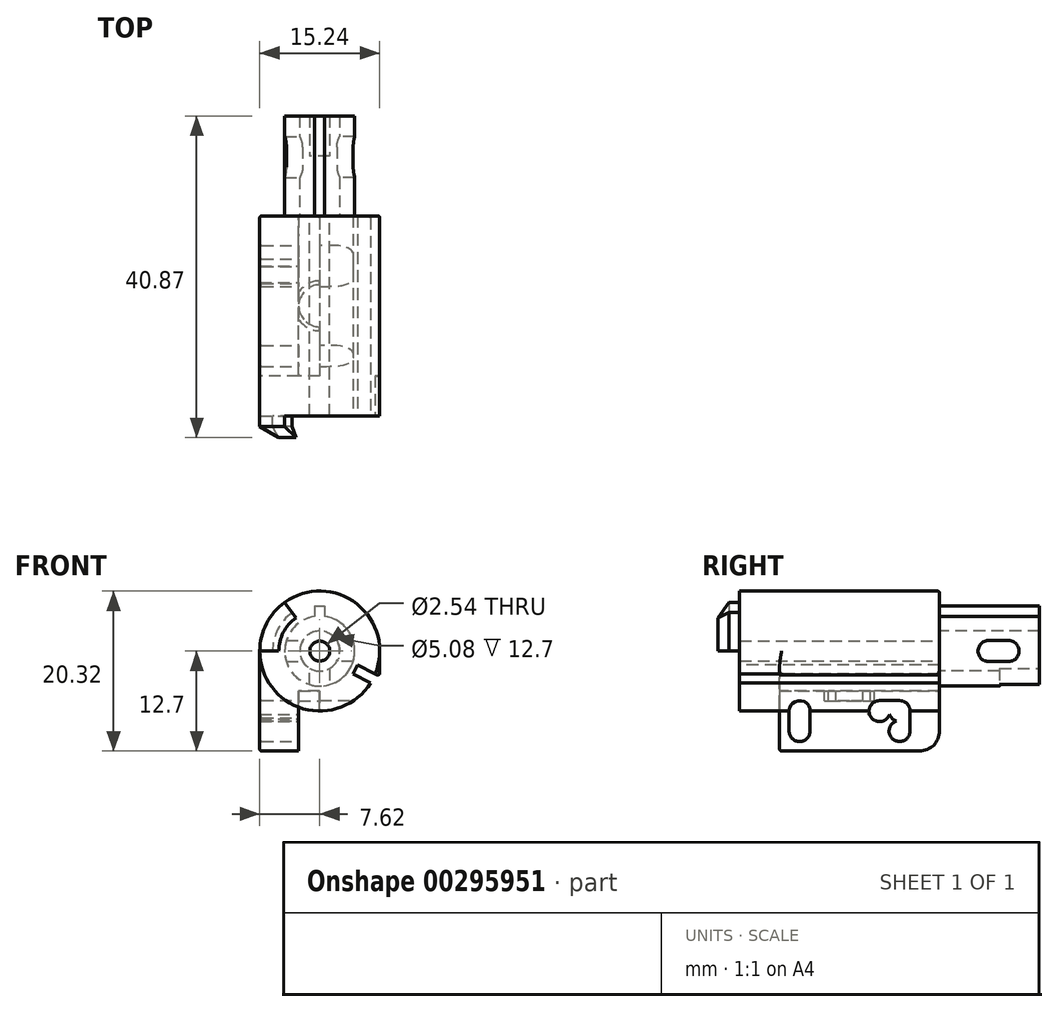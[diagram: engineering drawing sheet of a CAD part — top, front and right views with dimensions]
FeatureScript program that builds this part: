
annotation { "Feature Type Name" : "Feature", "Feature Type Description" : "" }
export const myFeature = defineFeature(function(context is Context, id is Id, definition is map)
    precondition{}
    {
        {
            var Q0;
            Q0=qCreatedBy(makeId("Front.planeOp"),FACE);
            var sketch = newSketch(context, id + "F0", { "sketchPlane" : qUnion([Q0])});
            skPoint(sketch, "E0.middle", {"position": v(0, 0) * mm});
            skLineSegment(sketch, "E1.bottom", {"start": v(7.62, 37.7) * mm, "end": v(-7.62, 37.7) * mm});
            skLineSegment(sketch, "E1.top", {"start": v(7.62, -37.7) * mm, "end": v(-7.62, -37.7) * mm});
            skLineSegment(sketch, "E1.left", {"start": v(7.62, 37.7) * mm, "end": v(7.62, -37.7) * mm});
            skLineSegment(sketch, "E1.right", {"start": v(-7.62, 37.7) * mm, "end": v(-7.62, -37.7) * mm});
            skCircle(sketch, "E2", {"center": v(0, 0) * mm, "radius": 7.62 * mm});
            skCircle(sketch, "E3", {"center": v(0, 0) * mm, "radius": 1.27 * mm});
            skSolve(sketch);
        }
        {
            var Q0;
            Q0=makeQuery(id+"F0.imprint","IMPRINT",FACE,{"disambiguationData":[TD([[makeQuery(id+"F0.imprint","IMPRINT",EDGE,{"derivedFrom":sQuery(id+"F0.wireOp",EDGE,"E3")}),-1.0]])]});
            extrude(context, id + "F1", {"entities" : qUnion([Q0]), "depth" : 12.7 * mm});
        }
        {
            var Q0;
            Q0=makeQuery(id+"F1.opExtrude","CAP_FACE",FACE,{"disambiguationData":[OSD([sQuery(id+"F0.wireOp",EDGE,"E2"),sQuery(id+"F0.wireOp",EDGE,"E3")])],"isStart":false});
            var sketch = newSketch(context, id + "F2", { "sketchPlane" : qUnion([Q0])});
            skArc(sketch, "E4", {"start": v(-7.62, 0) * mm, "mid": v(-6.78, 3.48) * mm, "end": v(-4.44, 6.2) * mm});
            skArc(sketch, "E5.0", {"start": v(-6, 0) * mm, "mid": v(-5.34, 2.74) * mm, "end": v(-3.5, 4.88) * mm});
            skLineSegment(sketch, "E6", {"start": v(-4.44, 6.2) * mm, "end": v(-3.5, 4.88) * mm});
            skLineSegment(sketch, "E7", {"start": v(-7.62, 0) * mm, "end": v(-6, 0) * mm});
            skSolve(sketch);
        }
        {
            var Q0;
            Q0=qSketchRegion(id+"F2",true);
            extrude(context, id + "F3", {"entities" : qUnion([Q0]), "operationType" : NewBodyOperationType.ADD, "depth" : 1.37 * mm});
        }
        {
            var Q0;
            Q0=makeQuery(id+"F3.opExtrude","CAP_FACE",FACE,{"disambiguationData":[OSD([sQuery(id+"F2.wireOp",EDGE,"E4"),sQuery(id+"F2.wireOp",EDGE,"E5.0"),sQuery(id+"F2.wireOp",EDGE,"E6"),sQuery(id+"F2.wireOp",EDGE,"E7")])],"isStart":false});
            cPlane(context, id + "F4", {"entities" : qUnion([Q0]), "cplaneType" : CPlaneType.OFFSET, "offset" : 1.4 * mm, "width" : 152.4 * mm, "height" : 152.4 * mm});
        }
        {
            var Q0;
            Q0=qCreatedBy(id+"F4.planeOp",FACE);
            var sketch = newSketch(context, id + "F5", { "sketchPlane" : qUnion([Q0])});
            skArc(sketch, "E8.0", {"start": v(-3.04, 4.23) * mm, "mid": v(-4.63, 2.38) * mm, "end": v(-5.2, 0) * mm});
            skSolve(sketch);
        }
        {
            var Q0;
            Q0=makeQuery(id+"F3.opExtrude","CAP_VERTEX",VERTEX,{"disambiguationData":[OSD([sQuery(id+"F0.wireOp",EDGE,"E2"),sQuery(id+"F2.wireOp",EDGE,"E4"),sQuery(id+"F2.wireOp",EDGE,"E7")])],"isStart":false});
            var Q1;
            Q1=makeQuery(id+"F3.opExtrude","CAP_VERTEX",VERTEX,{"disambiguationData":[OSD([sQuery(id+"F2.wireOp",EDGE,"E5.0"),sQuery(id+"F2.wireOp",EDGE,"E7")])],"isStart":false});
            var Q2;
            Q2=sQuery(id+"F5.wireOp",VERTEX,"E8.0.end");
            cPlane(context, id + "F6", {"entities" : qUnion([Q0, Q1, Q2]), "cplaneType" : CPlaneType.THREE_POINT, "offset" : 25.4 * mm, "width" : 152.4 * mm, "height" : 152.4 * mm});
        }
        {
            var Q0;
            Q0=qCreatedBy(id+"F6.planeOp",FACE);
            var sketch = newSketch(context, id + "F7", { "sketchPlane" : qUnion([Q0])});
            skPoint(sketch, "E9.0", {"position": v(-7.62, -14.07) * mm});
            skPoint(sketch, "E10.0", {"position": v(-6, -14.07) * mm});
            skPoint(sketch, "E11.0", {"position": v(-5.2, -15.47) * mm});
            skLineSegment(sketch, "E12", {"start": v(-7.62, -14.07) * mm, "end": v(-5.2, -15.47) * mm});
            skLineSegment(sketch, "E13", {"start": v(-5.2, -15.47) * mm, "end": v(-6, -14.07) * mm});
            skLineSegment(sketch, "E14", {"start": v(-6, -14.07) * mm, "end": v(-7.62, -14.07) * mm});
            skSolve(sketch);
        }
        {
            var Q0;
            Q0=makeQuery(id+"F3.opExtrude","CAP_VERTEX",VERTEX,{"disambiguationData":[OSD([sQuery(id+"F0.wireOp",EDGE,"E2"),sQuery(id+"F2.wireOp",EDGE,"E4"),sQuery(id+"F2.wireOp",EDGE,"E6")])],"isStart":false});
            var Q1;
            Q1=makeQuery(id+"F3.opExtrude","CAP_VERTEX",VERTEX,{"disambiguationData":[OSD([sQuery(id+"F2.wireOp",EDGE,"E5.0"),sQuery(id+"F2.wireOp",EDGE,"E6")])],"isStart":false});
            var Q2;
            Q2=sQuery(id+"F5.wireOp",VERTEX,"E8.0.start");
            cPlane(context, id + "F8", {"entities" : qUnion([Q0, Q1, Q2]), "cplaneType" : CPlaneType.THREE_POINT, "offset" : 25.4 * mm, "width" : 152.4 * mm, "height" : 152.4 * mm});
        }
        {
            var Q0;
            Q0=qCreatedBy(id+"F8.planeOp",FACE);
            var sketch = newSketch(context, id + "F9", { "sketchPlane" : qUnion([Q0])});
            skPoint(sketch, "E15.0", {"position": v(-14.07, 7.62) * mm});
            skPoint(sketch, "E16.0", {"position": v(-14.07, 6) * mm});
            skPoint(sketch, "E17.0", {"position": v(-15.47, 5.2) * mm});
            skLineSegment(sketch, "E18", {"start": v(-14.07, 7.62) * mm, "end": v(-14.07, 6) * mm});
            skLineSegment(sketch, "E19", {"start": v(-14.07, 6) * mm, "end": v(-15.47, 5.2) * mm});
            skLineSegment(sketch, "E20", {"start": v(-15.47, 5.2) * mm, "end": v(-14.07, 7.62) * mm});
            skSolve(sketch);
        }
        {
            var Q0;
            Q0=makeQuery(id+"F7.imprint","IMPRINT",FACE,{"disambiguationData":[TD([[makeQuery(id+"F7.imprint","IMPRINT",EDGE,{"derivedFrom":sQuery(id+"F7.wireOp",EDGE,"E12")}),1.0]])]});
            var Q1;
            Q1=makeQuery(id+"F9.imprint","IMPRINT",FACE,{"disambiguationData":[TD([[makeQuery(id+"F9.imprint","IMPRINT",EDGE,{"derivedFrom":sQuery(id+"F9.wireOp",EDGE,"E18")}),-1.0]])]});
            var Q2;
            Q2=makeQuery(id+"F7.imprint","IMPRINT",FACE,{"disambiguationData":[TD([[makeQuery(id+"F7.imprint","IMPRINT",EDGE,{"derivedFrom":sQuery(id+"F7.wireOp",EDGE,"E12")}),1.0]])]});
            var Q3;
            Q3=makeQuery(id+"F9.imprint","IMPRINT",FACE,{"disambiguationData":[TD([[makeQuery(id+"F9.imprint","IMPRINT",EDGE,{"derivedFrom":sQuery(id+"F9.wireOp",EDGE,"E18")}),-1.0]])]});
            var Q4;
            Q4=makeQuery(id+"F3.opExtrude","CAP_EDGE",EDGE,{"disambiguationData":[OSD([sQuery(id+"F2.wireOp",EDGE,"E4")])],"isStart":false});
            var Q5;
            Q5=makeQuery(id+"F3.opExtrude","CAP_EDGE",EDGE,{"disambiguationData":[OSD([sQuery(id+"F2.wireOp",EDGE,"E5.0")])],"isStart":false});
            var Q6;
            Q6=sQuery(id+"F5.wireOp",EDGE,"E8.0");
            loft(context, id + "F10", {"addGuides" : true, "sheetProfilesArray" : [{ "sheetProfileEntities" : qUnion([Q0]) }, { "sheetProfileEntities" : qUnion([Q1]) }], "wireProfilesArray" : [{ "wireProfileEntities" : qUnion([Q2]) }, { "wireProfileEntities" : qUnion([Q3]) }], "guidesArray" : [{ "guideEntities" : qUnion([Q4]), "guideDerivativeType" : LoftGuideDerivativeType.DEFAULT, "guideDerivativeMagnitude" : 1 }, { "guideEntities" : qUnion([Q5]), "guideDerivativeType" : LoftGuideDerivativeType.DEFAULT, "guideDerivativeMagnitude" : 1 }, { "guideEntities" : qUnion([Q6]), "guideDerivativeType" : LoftGuideDerivativeType.DEFAULT, "guideDerivativeMagnitude" : 1 }]});
        }
        {
            var Q0;
            Q0=makeQuery(id+"F1.opExtrude","CAP_FACE",FACE,{"disambiguationData":[OSD([sQuery(id+"F0.wireOp",EDGE,"E2"),sQuery(id+"F0.wireOp",EDGE,"E3")])],"isStart":true});
            var sketch = newSketch(context, id + "F11", { "sketchPlane" : qUnion([Q0])});
            skArc(sketch, "E21.0", {"start": v(-4.16, -6.39) * mm, "mid": v(-6.39, 4.16) * mm, "end": v(4.16, 6.39) * mm});
            skCircle(sketch, "E22", {"center": v(0, 0) * mm, "radius": 7.62 * mm});
            skSolve(sketch);
        }
        {
            var Q0;
            Q0=makeQuery(id+"F11.imprint","IMPRINT",FACE,{"disambiguationData":[TD([[makeQuery(id+"F11.imprint","IMPRINT",EDGE,{"derivedFrom":sQuery(id+"F11.wireOp",EDGE,"E22")}),1.0]])]});
            var Q1;
            Q1=makeQuery(id+"F11.imprint","IMPRINT",FACE,{"disambiguationData":[TD([[makeQuery(id+"F11.imprint","IMPRINT",EDGE,{"derivedFrom":makeQuery(id+"F1.opExtrude","CAP_EDGE",EDGE,{"disambiguationData":[OSD([sQuery(id+"F0.wireOp",EDGE,"E2")])],"isStart":true})}),-1.0]])]});
            var Q2;
            Q2=makeQuery(id+"F11.imprint","IMPRINT",FACE,{"disambiguationData":[TD([[makeQuery(id+"F11.imprint","IMPRINT",EDGE,{"derivedFrom":sQuery(id+"F11.wireOp",EDGE,"E22")}),-1.0]])]});
            extrude(context, id + "F12", {"entities" : qUnion([Q0, Q1, Q2]), "depth" : 12.7 * mm});
        }
        {
            var Q0;
            Q0=makeQuery(id+"FqKjOTA0KTiobea_0.opExtrude","SWEPT_BODY",BODY,{"disambiguationData":[OSD([sQuery(id+"F0.wireOp",EDGE,"uHF2WHmJ-zJ7i-FEed-3bSX-mTsy0IzEVw90"),sQuery(id+"F0.wireOp",EDGE,"k3DuiY5w-GI1o-rOdS-LLCr-VDr8IVeulzbr"),sQuery(id+"F0.wireOp",EDGE,"E1.left"),sQuery(id+"F0.wireOp",EDGE,"E1.right")])]});
            var Q1;
            Q1=makeQuery(id+"F1.opExtrude","SWEPT_BODY",BODY,{"disambiguationData":[OSD([sQuery(id+"F0.wireOp",EDGE,"E2"),sQuery(id+"F0.wireOp",EDGE,"E3")])]});
            var Q2;
            Q2=makeQuery(id+"F10.opLoft","SWEPT_BODY",BODY,{"disambiguationData":[OSD([sQuery(id+"F2.wireOp",EDGE,"E4"),sQuery(id+"F2.wireOp",EDGE,"E5.0"),sQuery(id+"F5.wireOp",EDGE,"E8.0"),makeQuery(id+"F7.imprint","IMPRINT",FACE,{"disambiguationData":[TD([[makeQuery(id+"F7.imprint","IMPRINT",EDGE,{"derivedFrom":sQuery(id+"F7.wireOp",EDGE,"E12")}),1.0]])]}),makeQuery(id+"F9.imprint","IMPRINT",FACE,{"disambiguationData":[TD([[makeQuery(id+"F9.imprint","IMPRINT",EDGE,{"derivedFrom":sQuery(id+"F9.wireOp",EDGE,"E18")}),-1.0]])]})])]});
            var Q3;
            Q3=makeQuery(id+"F12.opExtrude","SWEPT_BODY",BODY,{"disambiguationData":[OSD([sQuery(id+"F0.wireOp",EDGE,"E3"),sQuery(id+"F11.wireOp",EDGE,"E22")])]});
            booleanBodies(context, id + "F13", {"operationType" : BooleanOperationType.UNION, "tools" : qUnion([Q0, Q1, Q2, Q3])});
        }
        {
            var Q0;
            Q0=makeQuery(id+"F12.opExtrude","CAP_FACE",FACE,{"disambiguationData":[OSD([sQuery(id+"F0.wireOp",EDGE,"E3"),sQuery(id+"F11.wireOp",EDGE,"E22")])],"isStart":false});
            var sketch = newSketch(context, id + "F14", { "sketchPlane" : qUnion([Q0])});
            skCircle(sketch, "E23", {"center": v(0, 0) * mm, "radius": 7.62 * mm});
            skSolve(sketch);
        }
        {
            var Q0;
            Q0=makeQuery(id+"F14.imprint","IMPRINT",FACE,{"disambiguationData":[TD([[makeQuery(id+"F14.imprint","IMPRINT",EDGE,{"derivedFrom":sQuery(id+"F14.wireOp",EDGE,"E23")}),-1.0]])]});
            var sketch = newSketch(context, id + "F15", { "sketchPlane" : qUnion([Q0])});
            skCircle(sketch, "E24", {"center": v(0, 0) * mm, "radius": 4.45 * mm});
            skCircle(sketch, "E25", {"center": v(0, 0) * mm, "radius": 2.54 * mm});
            skSolve(sketch);
        }
        {
            var Q0;
            Q0=makeQuery(id+"F15.imprint","IMPRINT",FACE,{"disambiguationData":[TD([[makeQuery(id+"F15.imprint","IMPRINT",EDGE,{"derivedFrom":sQuery(id+"F15.wireOp",EDGE,"E24")}),1.0]])]});
            var Q1;
            Q1=qSketchRegion(id+"F17",true);
            extrude(context, id + "F16", {"entities" : qUnion([Q0, Q1]), "operationType" : NewBodyOperationType.ADD, "depth" : 12.7 * mm});
        }
        {
            var Q0;
            Q0=qCreatedBy(makeId("Right.planeOp"),FACE);
            var sketch = newSketch(context, id + "F17", { "sketchPlane" : qUnion([Q0])});
            skArc(sketch, "E26", {"start": v(18.92, 1.33) * mm, "mid": v(17.59, 0) * mm, "end": v(18.92, -1.33) * mm});
            skArc(sketch, "E27", {"start": v(21.46, -1.33) * mm, "mid": v(22.8, 0) * mm, "end": v(21.46, 1.33) * mm});
            skLineSegment(sketch, "E28", {"start": v(21.46, 0) * mm, "end": v(21.46, 1.33) * mm});
            skLineSegment(sketch, "E29", {"start": v(21.46, 1.33) * mm, "end": v(18.92, 1.33) * mm});
            skLineSegment(sketch, "E30", {"start": v(18.92, 1.33) * mm, "end": v(18.92, 0) * mm});
            skLineSegment(sketch, "E31", {"start": v(21.46, 0) * mm, "end": v(21.46, -1.33) * mm});
            skLineSegment(sketch, "E32", {"start": v(21.46, -1.33) * mm, "end": v(18.92, -1.33) * mm});
            skLineSegment(sketch, "E33", {"start": v(18.92, -1.33) * mm, "end": v(18.92, 0) * mm});
            skSolve(sketch);
        }
        {
            var Q0;
            Q0 = qSketchRegion(id + "F17", true);
            extrude(context, id + "F18", {"entities" : qUnion([Q0]), "operationType" : NewBodyOperationType.REMOVE, "oppositeDirection" : true, "depth" : 25.4 * mm});
        }
        {
            var Q0;
            Q0 = qSketchRegion(id + "F17", true);
            var Q1;
            {var subQ0=sQuery(id+"F17.wireOp",EDGE,"E27");var subQ1=sQuery(id+"F17.wireOp",EDGE,"E26");var subQ2=makeQuery(id+"F17.imprint","INTERSECT",VERTEX,{"disambiguationData":[OD(0.0)],"derivedFrom":[subQ1,subQ0]});Q1=makeQuery(id+"F17.imprint","IMPRINT",FACE,{"disambiguationData":[TD([[makeQuery(id+"F17.imprint","IMPRINT",EDGE,{"disambiguationData":[TD([[subQ2,1.0]])],"derivedFrom":subQ1}),1.0]])]});}
            extrude(context, id + "F19", {"entities" : qUnion([Q0, Q1]), "operationType" : NewBodyOperationType.REMOVE, "depth" : 25.4 * mm});
        }
        {
            var Q0;
            Q0=makeQuery(id+"F16.opExtrude","CAP_FACE",FACE,{"disambiguationData":[OSD([sQuery(id+"F15.wireOp",EDGE,"E24"),sQuery(id+"F15.wireOp",EDGE,"E25")])],"isStart":false});
            var sketch = newSketch(context, id + "F20", { "sketchPlane" : qUnion([Q0])});
            skLineSegment(sketch, "E34", {"start": v(0, -2.54) * mm, "end": v(0, -4.45) * mm});
            skLineSegment(sketch, "E35", {"start": v(0, -4.45) * mm, "end": v(-1.27, -4.45) * mm});
            skLineSegment(sketch, "E36", {"start": v(-1.27, -4.45) * mm, "end": v(1.27, -4.45) * mm});
            skLineSegment(sketch, "E37", {"start": v(1.27, -4.45) * mm, "end": v(1.27, -2.2) * mm});
            skLineSegment(sketch, "E38", {"start": v(1.27, -2.2) * mm, "end": v(-1.27, -2.2) * mm});
            skLineSegment(sketch, "E39", {"start": v(-1.27, -2.2) * mm, "end": v(-1.27, -4.45) * mm});
            skSolve(sketch);
        }
        {
            var Q0;
            {var subQ0=sQuery(id+"F20.wireOp",EDGE,"E36");var subQ3=sQuery(id+"F20.wireOp",EDGE,"E39");var subQ4=makeQuery(id+"F20.imprint","INTERSECT",VERTEX,{"derivedFrom":[subQ0,subQ3]});Q0=makeQuery(id+"F20.imprint","IMPRINT",FACE,{"disambiguationData":[TD([[makeQuery(id+"F20.imprint","IMPRINT",EDGE,{"disambiguationData":[TD([[subQ4,1.0]])],"derivedFrom":subQ3}),1.0]])]});}
            var Q1;
            {var subQ0=sQuery(id+"F20.wireOp",EDGE,"E36");var subQ3=sQuery(id+"F20.wireOp",EDGE,"E37");var subQ4=makeQuery(id+"F20.imprint","INTERSECT",VERTEX,{"derivedFrom":[subQ0,subQ3]});Q1=makeQuery(id+"F20.imprint","IMPRINT",FACE,{"disambiguationData":[TD([[makeQuery(id+"F20.imprint","IMPRINT",EDGE,{"disambiguationData":[TD([[subQ4,-1.0]])],"derivedFrom":subQ3}),1.0]])]});}
            var Q2;
            {var subQ0=sQuery(id+"F20.wireOp",EDGE,"E38");Q2=makeQuery(id+"F20.imprint","IMPRINT",FACE,{"disambiguationData":[TD([[makeQuery(id+"F20.imprint","IMPRINT",EDGE,{"derivedFrom":subQ0}),1.0]])]});}
            var Q3;
            {var subQ0=sQuery(id+"F20.wireOp",EDGE,"E34");Q3=makeQuery(id+"F20.imprint","IMPRINT",FACE,{"disambiguationData":[TD([[makeQuery(id+"F20.imprint","IMPRINT",EDGE,{"derivedFrom":subQ0}),1.0]])]});}
            var Q4;
            {var subQ0=sQuery(id+"F20.wireOp",EDGE,"E34");Q4=makeQuery(id+"F20.imprint","IMPRINT",FACE,{"disambiguationData":[TD([[makeQuery(id+"F20.imprint","IMPRINT",EDGE,{"derivedFrom":subQ0}),-1.0]])]});}
            extrude(context, id + "F21", {"entities" : qUnion([Q0, Q1, Q2, Q3, Q4]), "operationType" : NewBodyOperationType.REMOVE, "oppositeDirection" : true, "depth" : 5.08 * mm});
        }
        {
            var Q0;
            Q0=makeQuery(id+"F16.opExtrude","CAP_FACE",FACE,{"disambiguationData":[OSD([sQuery(id+"F15.wireOp",EDGE,"E24"),sQuery(id+"F15.wireOp",EDGE,"E25")])],"isStart":false});
            var sketch = newSketch(context, id + "F22", { "sketchPlane" : qUnion([Q0])});
            skLineSegment(sketch, "E40", {"start": v(0, 4.45) * mm, "end": v(0, 5.72) * mm});
            skPoint(sketch, "E40.endSnap0", {"position": v(0, 4.45) * mm});
            skLineSegment(sketch, "E41", {"start": v(0, 5.72) * mm, "end": v(0.64, 5.72) * mm});
            skLineSegment(sketch, "E42", {"start": v(0.64, 5.72) * mm, "end": v(-0.64, 5.72) * mm});
            skLineSegment(sketch, "E43", {"start": v(-0.64, 5.72) * mm, "end": v(-0.64, 4.4) * mm});
            skLineSegment(sketch, "E44", {"start": v(0.64, 5.72) * mm, "end": v(0.64, 4.4) * mm});
            skSolve(sketch);
        }
        {
            var Q0;
            {var subQ0=sQuery(id+"F22.wireOp",EDGE,"E40");Q0=makeQuery(id+"F22.imprint","IMPRINT",FACE,{"disambiguationData":[TD([[makeQuery(id+"F22.imprint","IMPRINT",EDGE,{"derivedFrom":subQ0}),1.0]])]});}
            var Q1;
            {var subQ0=sQuery(id+"F22.wireOp",EDGE,"E40");Q1=makeQuery(id+"F22.imprint","IMPRINT",FACE,{"disambiguationData":[TD([[makeQuery(id+"F22.imprint","IMPRINT",EDGE,{"derivedFrom":subQ0}),1.0]])]});}
            var Q2;
            {var subQ0=sQuery(id+"F22.wireOp",EDGE,"E40");Q2=makeQuery(id+"F22.imprint","IMPRINT",FACE,{"disambiguationData":[TD([[makeQuery(id+"F22.imprint","IMPRINT",EDGE,{"derivedFrom":subQ0}),-1.0]])]});}
            extrude(context, id + "F23", {"entities" : qUnion([Q0, Q1, Q2]), "operationType" : NewBodyOperationType.ADD, "oppositeDirection" : true, "depth" : 12.7 * mm});
        }
        {
            var Q0;
            Q0=makeQuery(id+"F1.opExtrude","CAP_FACE",FACE,{"disambiguationData":[OSD([sQuery(id+"F0.wireOp",EDGE,"E2"),sQuery(id+"F0.wireOp",EDGE,"E3")])],"isStart":false});
            var sketch = newSketch(context, id + "F24", { "sketchPlane" : qUnion([Q0])});
            skLineSegment(sketch, "E45", {"start": v(-5.34, 2.74) * mm, "end": v(0, 0) * mm});
            skLineSegment(sketch, "E46", {"start": v(4.52, -2.32) * mm, "end": v(4.8, -1.75) * mm});
            skLineSegment(sketch, "E47", {"start": v(4.8, -1.75) * mm, "end": v(4.23, -2.88) * mm});
            skLineSegment(sketch, "E48", {"start": v(4.8, -1.75) * mm, "end": v(7.05, -2.9) * mm});
            skLineSegment(sketch, "E49", {"start": v(4.23, -2.88) * mm, "end": v(6.47, -4.03) * mm});
            skLineSegment(sketch, "E50", {"start": v(0, 0) * mm, "end": v(4.52, -2.32) * mm});
            skLineSegment(sketch, "E51", {"start": v(4.52, -2.32) * mm, "end": v(6.78, -3.48) * mm});
            skSolve(sketch);
        }
        {
            var Q0;
            {var subQ0=sQuery(id+"F24.wireOp",EDGE,"E48");Q0=makeQuery(id+"F24.imprint","IMPRINT",FACE,{"disambiguationData":[TD([[makeQuery(id+"F24.imprint","IMPRINT",EDGE,{"derivedFrom":subQ0}),-1.0]])]});}
            var Q1;
            {var subQ0=sQuery(id+"F24.wireOp",EDGE,"E49");Q1=makeQuery(id+"F24.imprint","IMPRINT",FACE,{"disambiguationData":[TD([[makeQuery(id+"F24.imprint","IMPRINT",EDGE,{"derivedFrom":subQ0}),1.0]])]});}
            extrude(context, id + "F25", {"entities" : qUnion([Q0, Q1]), "operationType" : NewBodyOperationType.REMOVE, "oppositeDirection" : true, "depth" : 25.4 * mm});
        }
        {
            var Q0;
            Q0=makeQuery(id+"F14.imprint","IMPRINT",FACE,{"disambiguationData":[TD([[makeQuery(id+"F14.imprint","IMPRINT",EDGE,{"derivedFrom":sQuery(id+"F14.wireOp",EDGE,"E23")}),-1.0]])]});
            cPlane(context, id + "F26", {"entities" : qUnion([Q0]), "cplaneType" : CPlaneType.OFFSET, "offset" : 20.32 * mm, "oppositeDirection" : true, "width" : 152.4 * mm, "height" : 152.4 * mm});
        }
        {
            var Q0;
            Q0=qCreatedBy(id+"F26.planeOp",FACE);
            var sketch = newSketch(context, id + "F27", { "sketchPlane" : qUnion([Q0])});
            skLineSegment(sketch, "E52.0.0", {"start": v(-6.47, -4.03) * mm, "end": v(-4.23, -2.88) * mm});
            skLineSegment(sketch, "E52.0.1", {"start": v(-4.23, -2.88) * mm, "end": v(-4.8, -1.75) * mm});
            skLineSegment(sketch, "E52.0.2", {"start": v(-4.8, -1.75) * mm, "end": v(-7.05, -2.9) * mm});
            skArc(sketch, "E52.0.3", {"start": v(-7.05, -2.9) * mm, "mid": v(-4.73, 5.97) * mm, "end": v(4.44, 6.2) * mm});
            skLineSegment(sketch, "E52.0.4", {"start": v(4.44, 6.2) * mm, "end": v(3.5, 4.88) * mm});
            skArc(sketch, "E52.0.5", {"start": v(3.5, 4.88) * mm, "mid": v(5.34, 2.74) * mm, "end": v(6, 0) * mm});
            skLineSegment(sketch, "E52.0.6", {"start": v(6, 0) * mm, "end": v(7.62, 0) * mm});
            skArc(sketch, "E52.0.7", {"start": v(7.62, 0) * mm, "mid": v(2.1, -7.33) * mm, "end": v(-6.47, -4.03) * mm});
            skLineSegment(sketch, "E53", {"start": v(0, 0) * mm, "end": v(-7.62, 0) * mm});
            skLineSegment(sketch, "E54", {"start": v(-7.62, 0) * mm, "end": v(7.62, 0) * mm});
            skLineSegment(sketch, "E55", {"start": v(7.62, 0) * mm, "end": v(7.62, -12.7) * mm});
            skLineSegment(sketch, "E56", {"start": v(-7.62, 0) * mm, "end": v(-7.62, -12.7) * mm});
            skLineSegment(sketch, "E57", {"start": v(-7.62, -12.7) * mm, "end": v(7.62, -12.7) * mm});
            skLineSegment(sketch, "E58", {"start": v(0, 0) * mm, "end": v(0, -12.7) * mm});
            skLineSegment(sketch, "E59", {"start": v(-4.8, -1.75) * mm, "end": v(-7.62, -3.2) * mm});
            skLineSegment(sketch, "E60", {"start": v(-4.8, -1.75) * mm, "end": v(-4.23, -2.88) * mm});
            skLineSegment(sketch, "E61", {"start": v(-4.23, -2.88) * mm, "end": v(-7.62, -4.62) * mm});
            skPoint(sketch, "E61.endSnap0", {"position": v(-7.62, -6.35) * mm});
            skSolve(sketch);
        }
        {
            var Q0;
            {var subQ3=sQuery(id+"F27.wireOp",EDGE,"E52.0.7");var subQ5=sQuery(id+"F27.wireOp",EDGE,"E61");var subQ6=makeQuery(id+"F27.imprint","INTERSECT",VERTEX,{"derivedFrom":[subQ3,subQ5]});Q0=makeQuery(id+"F27.imprint","IMPRINT",FACE,{"disambiguationData":[TD([[makeQuery(id+"F27.imprint","IMPRINT",EDGE,{"disambiguationData":[TD([[subQ6,1.0]])],"derivedFrom":subQ3}),1.0]])]});}
            var Q1;
            {var subQ0=sQuery(id+"F27.wireOp",EDGE,"E55");Q1=makeQuery(id+"F27.imprint","IMPRINT",FACE,{"disambiguationData":[TD([[makeQuery(id+"F27.imprint","IMPRINT",EDGE,{"derivedFrom":subQ0}),-1.0]])]});}
            var Q2;
            {var subQ0=sQuery(id+"F27.wireOp",EDGE,"E59");var subQ1=sQuery(id+"F27.wireOp",EDGE,"E52.0.3");var subQ2=makeQuery(id+"F27.imprint","INTERSECT",VERTEX,{"derivedFrom":[subQ1,subQ0]});Q2=makeQuery(id+"F27.imprint","IMPRINT",FACE,{"disambiguationData":[TD([[makeQuery(id+"F27.imprint","IMPRINT",EDGE,{"disambiguationData":[TD([[subQ2,-1.0]])],"derivedFrom":subQ0}),-1.0]])]});}
            extrude(context, id + "F28", {"entities" : qUnion([Q0, Q1, Q2]), "operationType" : NewBodyOperationType.ADD, "depth" : 20.32 * mm});
        }
        {
            var Q0;
            Q0=makeQuery(id+"F28.opExtrude","SWEPT_FACE",FACE,{"disambiguationData":[OSD([sQuery(id+"F27.wireOp",EDGE,"E57")])]});
            var sketch = newSketch(context, id + "F29", { "sketchPlane" : qUnion([Q0])});
            skLineSegment(sketch, "E62", {"start": v(-2.67, 7.62) * mm, "end": v(-2.67, -12.7) * mm});
            skLineSegment(sketch, "E63", {"start": v(2.67, 7.62) * mm, "end": v(2.67, -12.7) * mm});
            skSolve(sketch);
        }
        {
            var Q0;
            Q0 = qSketchRegion(id + "F29", true);
            var Q1;
            {var subQ0=sQuery(id+"F29.wireOp",EDGE,"E62");Q1=makeQuery(id+"F29.imprint","IMPRINT",FACE,{"disambiguationData":[TD([[makeQuery(id+"F29.imprint","IMPRINT",EDGE,{"derivedFrom":subQ0}),1.0]])]});}
            extrude(context, id + "F30", {"entities" : qUnion([Q0, Q1]), "operationType" : NewBodyOperationType.REMOVE, "oppositeDirection" : true, "depth" : 7.62 * mm});
        }
        {
            var Q0;
            {var subQ0=sQuery(id+"F27.wireOp",EDGE,"E56");Q0=makeQuery(id+"F28.opExtrude","SWEPT_FACE",FACE,{"disambiguationData":[OSD([subQ0]),TDD([makeQuery(id+"F27.imprint","IMPRINT",EDGE,{"disambiguationData":[TD([[makeQuery(id+"F27.imprint","INTERSECT",VERTEX,{"derivedFrom":[subQ0,sQuery(id+"F27.wireOp",EDGE,"E57")]}),1.0]])],"derivedFrom":subQ0})])]});}
            var sketch = newSketch(context, id + "F31", { "sketchPlane" : qUnion([Q0])});
            skCircle(sketch, "E64", {"center": v(-5.08, -10.16) * mm, "radius": 1.33 * mm});
            skCircle(sketch, "E65", {"center": v(7.62, -10.16) * mm, "radius": 1.33 * mm});
            skCircle(sketch, "E66", {"center": v(7.62, -7.62) * mm, "radius": 1.33 * mm});
            skCircle(sketch, "E67", {"center": v(-5.08, -7.62) * mm, "radius": 1.33 * mm});
            skCircle(sketch, "E68", {"center": v(5.08, -7.62) * mm, "radius": 1.33 * mm});
            skLineSegment(sketch, "E69", {"start": v(4.08, -8.5) * mm, "end": v(6.68, -11.1) * mm});
            skLineSegment(sketch, "E70", {"start": v(6.68, -11.1) * mm, "end": v(4.08, -8.5) * mm});
            skLineSegment(sketch, "E71", {"start": v(7.62, -7.62) * mm, "end": v(8.95, -7.62) * mm});
            skLineSegment(sketch, "E72", {"start": v(8.95, -7.62) * mm, "end": v(8.95, -10.16) * mm});
            skLineSegment(sketch, "E73", {"start": v(7.62, -7.62) * mm, "end": v(7.62, -6.29) * mm});
            skLineSegment(sketch, "E74", {"start": v(7.62, -6.29) * mm, "end": v(5.08, -6.29) * mm});
            skLineSegment(sketch, "E75", {"start": v(-5.08, -7.62) * mm, "end": v(-3.75, -7.62) * mm});
            skLineSegment(sketch, "E76", {"start": v(-3.75, -7.62) * mm, "end": v(-3.75, -10.16) * mm});
            skLineSegment(sketch, "E77", {"start": v(-3.75, -10.16) * mm, "end": v(-6.41, -10.16) * mm});
            skLineSegment(sketch, "E78", {"start": v(-6.41, -10.16) * mm, "end": v(-6.41, -7.62) * mm});
            skSolve(sketch);
        }
        {
            var Q0;
            {var subQ0=sQuery(id+"F31.wireOp",EDGE,"E67");var subQ1=makeQuery(id+"F31.imprint","INTERSECT",VERTEX,{"derivedFrom":[subQ0,sQuery(id+"F31.wireOp",EDGE,"E76")]});Q0=makeQuery(id+"F31.imprint","IMPRINT",FACE,{"disambiguationData":[TD([[makeQuery(id+"F31.imprint","IMPRINT",EDGE,{"disambiguationData":[TD([[subQ1,-1.0]])],"derivedFrom":subQ0}),1.0]])]});}
            var Q1;
            {var subQ0=sQuery(id+"F31.wireOp",EDGE,"E77");Q1=makeQuery(id+"F31.imprint","IMPRINT",FACE,{"disambiguationData":[TD([[makeQuery(id+"F31.imprint","IMPRINT",EDGE,{"derivedFrom":subQ0}),1.0]])]});}
            var Q2;
            {var subQ0=sQuery(id+"F31.wireOp",EDGE,"E76");Q2=makeQuery(id+"F31.imprint","IMPRINT",FACE,{"disambiguationData":[TD([[makeQuery(id+"F31.imprint","IMPRINT",EDGE,{"derivedFrom":subQ0}),-1.0]])]});}
            var Q3;
            {var subQ0=sQuery(id+"F31.wireOp",EDGE,"E78");Q3=makeQuery(id+"F31.imprint","IMPRINT",FACE,{"disambiguationData":[TD([[makeQuery(id+"F31.imprint","IMPRINT",EDGE,{"derivedFrom":subQ0}),-1.0]])]});}
            var Q4;
            {var subQ0=sQuery(id+"F31.wireOp",EDGE,"E70");var subQ1=sQuery(id+"F31.wireOp",EDGE,"E65");var subQ2=makeQuery(id+"F31.imprint","INTERSECT",VERTEX,{"derivedFrom":[subQ1,subQ0]});Q4=makeQuery(id+"F31.imprint","IMPRINT",FACE,{"disambiguationData":[TD([[makeQuery(id+"F31.imprint","IMPRINT",EDGE,{"disambiguationData":[TD([[subQ2,1.0]])],"derivedFrom":subQ1}),-1.0]])]});}
            var Q5;
            {var subQ0=sQuery(id+"F31.wireOp",EDGE,"E74");Q5=makeQuery(id+"F31.imprint","IMPRINT",FACE,{"disambiguationData":[TD([[makeQuery(id+"F31.imprint","IMPRINT",EDGE,{"derivedFrom":subQ0}),1.0]])]});}
            var Q6;
            {var subQ0=sQuery(id+"F31.wireOp",EDGE,"E71");Q6=makeQuery(id+"F31.imprint","IMPRINT",FACE,{"disambiguationData":[TD([[makeQuery(id+"F31.imprint","IMPRINT",EDGE,{"derivedFrom":subQ0}),-1.0]])]});}
            var Q7;
            {var subQ0=sQuery(id+"F31.wireOp",EDGE,"E71");Q7=makeQuery(id+"F31.imprint","IMPRINT",FACE,{"disambiguationData":[TD([[makeQuery(id+"F31.imprint","IMPRINT",EDGE,{"derivedFrom":subQ0}),1.0]])]});}
            var Q8;
            {var subQ0=sQuery(id+"F31.wireOp",EDGE,"E65");var subQ1=makeQuery(id+"F31.imprint","INTERSECT",VERTEX,{"derivedFrom":[subQ0,sQuery(id+"F31.wireOp",EDGE,"E72")]});Q8=makeQuery(id+"F31.imprint","IMPRINT",FACE,{"disambiguationData":[TD([[makeQuery(id+"F31.imprint","IMPRINT",EDGE,{"disambiguationData":[TD([[subQ1,-1.0]])],"derivedFrom":subQ0}),1.0]])]});}
            var Q9;
            {var subQ0=sQuery(id+"F31.wireOp",EDGE,"E72");Q9=makeQuery(id+"F31.imprint","IMPRINT",FACE,{"disambiguationData":[TD([[makeQuery(id+"F31.imprint","IMPRINT",EDGE,{"derivedFrom":subQ0}),-1.0]])]});}
            var Q10;
            {var subQ0=sQuery(id+"F31.wireOp",EDGE,"E68");var subQ1=sQuery(id+"F31.wireOp",EDGE,"E66");var subQ2=makeQuery(id+"F31.imprint","INTERSECT",VERTEX,{"disambiguationData":[OD(0.0)],"derivedFrom":[subQ1,subQ0]});Q10=makeQuery(id+"F31.imprint","IMPRINT",FACE,{"disambiguationData":[TD([[makeQuery(id+"F31.imprint","IMPRINT",EDGE,{"disambiguationData":[TD([[subQ2,-1.0]])],"derivedFrom":subQ1}),1.0]])]});}
            var Q11;
            {var subQ0=sQuery(id+"F31.wireOp",EDGE,"E66");var subQ1=sQuery(id+"F31.wireOp",EDGE,"E65");var subQ2=makeQuery(id+"F31.imprint","INTERSECT",VERTEX,{"disambiguationData":[OD(0.0)],"derivedFrom":[subQ1,subQ0]});Q11=makeQuery(id+"F31.imprint","IMPRINT",FACE,{"disambiguationData":[TD([[makeQuery(id+"F31.imprint","IMPRINT",EDGE,{"disambiguationData":[TD([[subQ2,-1.0]])],"derivedFrom":subQ1}),1.0]])]});}
            var Q12;
            {var subQ0=sQuery(id+"F31.wireOp",EDGE,"E68");var subQ1=sQuery(id+"F31.wireOp",EDGE,"E66");var subQ5=makeQuery(id+"F31.imprint","INTERSECT",VERTEX,{"disambiguationData":[OD(0.0)],"derivedFrom":[subQ1,subQ0]});Q12=makeQuery(id+"F31.imprint","IMPRINT",FACE,{"disambiguationData":[TD([[makeQuery(id+"F31.imprint","IMPRINT",EDGE,{"disambiguationData":[TD([[subQ5,-1.0]])],"derivedFrom":subQ1}),-1.0]])]});}
            var Q13;
            {var subQ0=sQuery(id+"F31.wireOp",EDGE,"E77");Q13=makeQuery(id+"F31.imprint","IMPRINT",FACE,{"disambiguationData":[TD([[makeQuery(id+"F31.imprint","IMPRINT",EDGE,{"derivedFrom":subQ0}),-1.0]])]});}
            var Q14;
            {var subQ0=sQuery(id+"F31.wireOp",EDGE,"E67");var subQ1=sQuery(id+"F31.wireOp",EDGE,"E64");var subQ2=makeQuery(id+"F31.imprint","INTERSECT",VERTEX,{"disambiguationData":[OD(0.0)],"derivedFrom":[subQ1,subQ0]});Q14=makeQuery(id+"F31.imprint","IMPRINT",FACE,{"disambiguationData":[TD([[makeQuery(id+"F31.imprint","IMPRINT",EDGE,{"disambiguationData":[TD([[subQ2,-1.0]])],"derivedFrom":subQ1}),1.0]])]});}
            extrude(context, id + "F32", {"entities" : qUnion([Q0, Q1, Q2, Q3, Q4, Q5, Q6, Q7, Q8, Q9, Q10, Q11, Q12, Q13, Q14]), "operationType" : NewBodyOperationType.REMOVE, "oppositeDirection" : true, "depth" : 25.4 * mm});
        }
        {
            var Q0;
            Q0=makeQuery(id+"F30.boolean.opBoolean","COPY",FACE,{"derivedFrom":makeQuery(id+"F30.opExtrude","CAP_FACE",FACE,{"disambiguationData":[OSD([sQuery(id+"F27.wireOp",EDGE,"E57"),sQuery(id+"F29.wireOp",EDGE,"E62"),sQuery(id+"F29.wireOp",EDGE,"E63")])],"isStart":false})});
            var sketch = newSketch(context, id + "F33", { "sketchPlane" : qUnion([Q0])});
            skLineSegment(sketch, "E79", {"start": v(0, 7.62) * mm, "end": v(0, -1.27) * mm});
            skLineSegment(sketch, "E80", {"start": v(0, -1.27) * mm, "end": v(0, -12.7) * mm});
            skCircle(sketch, "E81", {"center": v(0, -1.27) * mm, "radius": 2.67 * mm});
            skCircle(sketch, "E82", {"center": v(0, -1.27) * mm, "radius": 3.18 * mm});
            skSolve(sketch);
        }
        {
            var Q0;
            Q0 = qSketchRegion(id + "F33", true);
            extrude(context, id + "F34", {"entities" : qUnion([Q0]), "operationType" : NewBodyOperationType.ADD, "depth" : 1.27 * mm});
        }
        {
            var Q0;
            Q0=makeQuery(id+"F12.opExtrude","CAP_EDGE",EDGE,{"disambiguationData":[OSD([sQuery(id+"F11.wireOp",EDGE,"E22")])],"isStart":false});
            var Q1;
            {var subQ0=sQuery(id+"F27.wireOp",EDGE,"E56");Q1=makeQuery(id+"F28.opExtrude","CAP_EDGE",EDGE,{"disambiguationData":[OSD([subQ0]),TDD([makeQuery(id+"F27.imprint","IMPRINT",EDGE,{"disambiguationData":[TD([[makeQuery(id+"F27.imprint","INTERSECT",VERTEX,{"derivedFrom":[subQ0,sQuery(id+"F27.wireOp",EDGE,"E57")]}),1.0]])],"derivedFrom":subQ0})])],"isStart":true});}
            var Q2;
            Q2=makeQuery(id+"F28.opExtrude","SWEPT_EDGE",EDGE,{"disambiguationData":[OSD([sQuery(id+"F27.wireOp",EDGE,"E56"),sQuery(id+"F27.wireOp",EDGE,"E57")])]});
            var Q3;
            {var subQ0=sQuery(id+"F27.wireOp",EDGE,"E56");Q3=makeQuery(id+"F28.opExtrude","CAP_EDGE",EDGE,{"disambiguationData":[OSD([subQ0]),TDD([makeQuery(id+"F27.imprint","IMPRINT",EDGE,{"disambiguationData":[TD([[makeQuery(id+"F27.imprint","INTERSECT",VERTEX,{"derivedFrom":[subQ0,sQuery(id+"F27.wireOp",EDGE,"E57")]}),1.0]])],"derivedFrom":subQ0})])],"isStart":false});}
            var Q4;
            Q4=makeQuery(id+"F28.opExtrude","CAP_EDGE",EDGE,{"disambiguationData":[OSD([sQuery(id+"F27.wireOp",EDGE,"E55")])],"isStart":false});
            var Q5;
            Q5=makeQuery(id+"F28.opExtrude","SWEPT_EDGE",EDGE,{"disambiguationData":[OSD([sQuery(id+"F27.wireOp",EDGE,"E55"),sQuery(id+"F27.wireOp",EDGE,"E57")])]});
            var Q6;
            {var subQ1=sQuery(id+"F27.wireOp",EDGE,"E57");Q6=makeQuery(id+"F30.boolean.opBoolean","SPLIT",EDGE,{"disambiguationData":[TD([makeQuery(id+"F30.opExtrude","SWEPT_FACE",FACE,{"disambiguationData":[OSD([sQuery(id+"F29.wireOp",EDGE,"E63")])]})])],"derivedFrom":makeQuery(id+"F28.opExtrude","CAP_EDGE",EDGE,{"disambiguationData":[OSD([subQ1])],"isStart":true})});}
            var Q7;
            {var subQ0=sQuery(id+"F27.wireOp",EDGE,"E57");var subQ1=sQuery(id+"F27.wireOp",EDGE,"E55");Q7=makeQuery(id+"F30.boolean.opBoolean","SPLIT",EDGE,{"disambiguationData":[TD([makeQuery(id+"F28.opExtrude","SWEPT_FACE",FACE,{"disambiguationData":[OSD([subQ1])]})])],"derivedFrom":makeQuery(id+"F28.opExtrude","CAP_EDGE",EDGE,{"disambiguationData":[OSD([subQ0])],"isStart":true})});}
            var Q8;
            Q8=makeQuery(id+"F28.opExtrude","CAP_EDGE",EDGE,{"disambiguationData":[OSD([sQuery(id+"F27.wireOp",EDGE,"E55")])],"isStart":true});
            var Q9;
            Q9=makeQuery(id+"F25.boolean.opBoolean","COPY",EDGE,{"derivedFrom":makeQuery(id+"F25.opExtrude","CAP_EDGE",EDGE,{"disambiguationData":[OSD([sQuery(id+"F24.wireOp",EDGE,"E48")])],"isStart":false})});
            var Q10;
            Q10=makeQuery(id+"F25.boolean.opBoolean","COPY",EDGE,{"derivedFrom":makeQuery(id+"F25.opExtrude","CAP_EDGE",EDGE,{"disambiguationData":[OSD([sQuery(id+"F24.wireOp",EDGE,"E49")])],"isStart":false})});
            fillet(context, id + "F35", {"entities" : qUnion([Q0, Q1, Q2, Q3, Q4, Q5, Q6, Q7, Q8, Q9, Q10]), "radius" : 0.25 * mm, "tangentPropagation" : true, "allowEdgeOverflow" : false});
        }
        {
            var Q0;
            Q0=makeQuery(id+"F32.boolean.opBoolean","COPY",EDGE,{"derivedFrom":makeQuery(id+"F32.opExtrude","CAP_EDGE",EDGE,{"disambiguationData":[OSD([sQuery(id+"F31.wireOp",EDGE,"E74")])],"isStart":true})});
            var Q1;
            Q1=makeQuery(id+"F32.boolean.opBoolean","COPY",EDGE,{"derivedFrom":makeQuery(id+"F32.opExtrude","CAP_EDGE",EDGE,{"disambiguationData":[OSD([sQuery(id+"F31.wireOp",EDGE,"E76")])],"isStart":true})});
            var Q2;
            Q2=makeQuery(id+"F32.boolean.opBoolean","INTERSECT",EDGE,{"derivedFrom":[makeQuery(id+"F28.opExtrude","SWEPT_FACE",FACE,{"disambiguationData":[OSD([sQuery(id+"F27.wireOp",EDGE,"E55")])]}),makeQuery(id+"F32.opExtrude","SWEPT_FACE",FACE,{"disambiguationData":[OSD([sQuery(id+"F31.wireOp",EDGE,"E76")])]})]});
            var Q3;
            Q3=makeQuery(id+"F32.boolean.opBoolean","INTERSECT",EDGE,{"derivedFrom":[makeQuery(id+"F28.opExtrude","SWEPT_FACE",FACE,{"disambiguationData":[OSD([sQuery(id+"F27.wireOp",EDGE,"E55")])]}),makeQuery(id+"F32.opExtrude","SWEPT_FACE",FACE,{"disambiguationData":[OSD([sQuery(id+"F31.wireOp",EDGE,"E74")])]})]});
            fillet(context, id + "F36", {"entities" : qUnion([Q0, Q1, Q2, Q3]), "radius" : 0.25 * mm, "tangentPropagation" : true, "allowEdgeOverflow" : false});
        }
        {
            var Q0;
            {var subQ0=sQuery(id+"F27.wireOp",EDGE,"E57");Q0=makeQuery(id+"F30.boolean.opBoolean","SPLIT",EDGE,{"disambiguationData":[TD([makeQuery(id+"F30.opExtrude","SWEPT_FACE",FACE,{"disambiguationData":[OSD([sQuery(id+"F29.wireOp",EDGE,"E63")])]})])],"derivedFrom":makeQuery(id+"F28.opExtrude","CAP_EDGE",EDGE,{"disambiguationData":[OSD([subQ0])],"isStart":false})});}
            var Q1;
            {var subQ0=sQuery(id+"F27.wireOp",EDGE,"E55");var subQ1=sQuery(id+"F27.wireOp",EDGE,"E57");Q1=makeQuery(id+"F30.boolean.opBoolean","SPLIT",EDGE,{"disambiguationData":[TD([makeQuery(id+"F28.opExtrude","SWEPT_FACE",FACE,{"disambiguationData":[OSD([subQ0])]})])],"derivedFrom":makeQuery(id+"F28.opExtrude","CAP_EDGE",EDGE,{"disambiguationData":[OSD([subQ1])],"isStart":false})});}
            fillet(context, id + "F37", {"entities" : qUnion([Q0, Q1]), "radius" : 2.54 * mm, "tangentPropagation" : true, "allowEdgeOverflow" : false});
        }
    });
